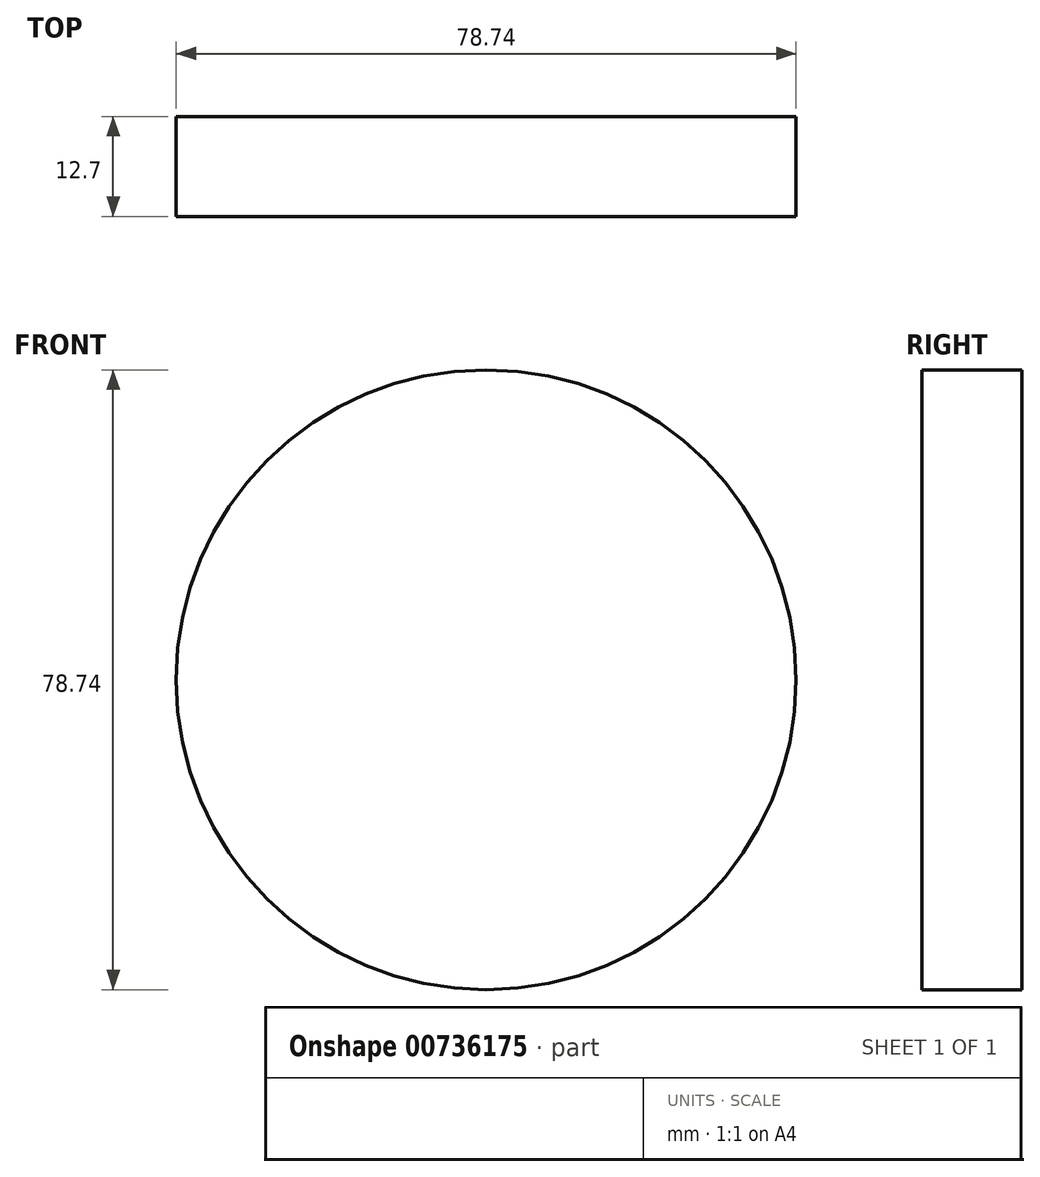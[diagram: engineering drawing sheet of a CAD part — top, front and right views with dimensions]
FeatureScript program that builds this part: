
annotation { "Feature Type Name" : "Feature", "Feature Type Description" : "" }
export const myFeature = defineFeature(function(context is Context, id is Id, definition is map)
    precondition{}
    {
        {
            var Q0;
            Q0=qCreatedBy(makeId("Front.planeOp"),FACE);
            var sketch = newSketch(context, id + "F0", { "sketchPlane" : qUnion([Q0])});
            skCircle(sketch, "E0", {"center": v(0, 0) * mm, "radius": 39.37 * mm});
            skSolve(sketch);
        }
        {
            var Q0;
            Q0=makeQuery(id+"F0.imprint","IMPRINT",FACE,{"disambiguationData":[TD([[makeQuery(id+"F0.imprint","IMPRINT",EDGE,{"derivedFrom":sQuery(id+"F0.wireOp",EDGE,"E0")}),1.0]])]});
            extrude(context, id + "F1", {"entities" : qUnion([Q0]), "depth" : 12.7 * mm, "offsetDistance" : 25.4 * mm});
        }
    });
